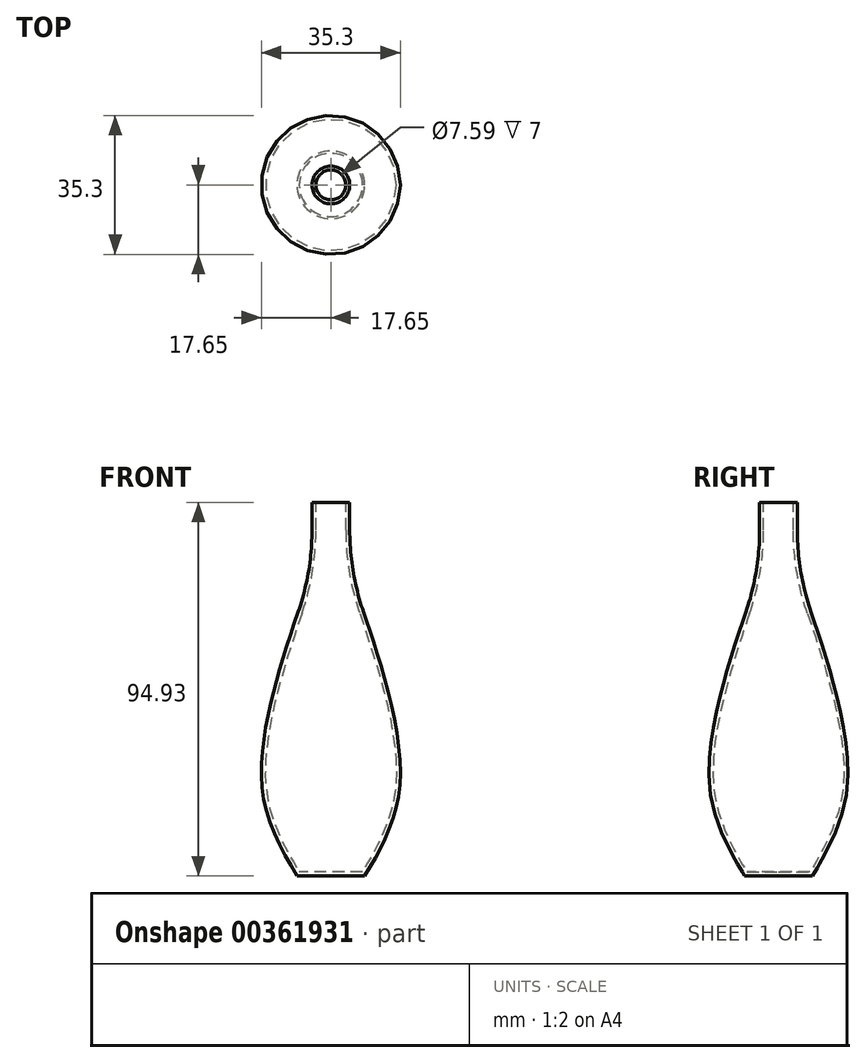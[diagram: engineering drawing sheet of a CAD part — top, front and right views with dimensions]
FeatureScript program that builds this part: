
annotation { "Feature Type Name" : "Feature", "Feature Type Description" : "" }
export const myFeature = defineFeature(function(context is Context, id is Id, definition is map)
    precondition{}
    {
        {
            var Q0;
            Q0=qCreatedBy(makeId("Front.planeOp"),FACE);
            var sketch = newSketch(context, id + "F0", { "sketchPlane" : qUnion([Q0])});
            skLineSegment(sketch, "E0", {"start": v(0, -43.14) * mm, "end": v(8.6, -43.14) * mm});
            skLineSegment(sketch, "E1", {"start": v(4.8, 43) * mm, "end": v(4.8, 51.79) * mm});
            skLineSegment(sketch, "E2", {"start": v(4.8, 51.79) * mm, "end": v(0, 51.79) * mm});
            skLineSegment(sketch, "E3", {"start": v(0, 55.64) * mm, "end": v(0, -43.14) * mm});
            skLineSegment(sketch, "E4", {"start": v(4.8, 33.68) * mm, "end": v(4.8, 43) * mm});
            skFitSpline(sketch, "E5", {"points": [v(4.8, 33.68) * mm, v(10.38, 17.7) * mm, v(17.57, -19.3) * mm, v(8.6, -43.14) * mm], "startDerivative": vector(18.72, -51.04) * mm, "endDerivative": vector(-38.07, -64.94) * mm});
            skSolve(sketch);
        }
        {
            var Q0;
            {var subQ1=sQuery(id+"F0.wireOp",EDGE,"E0");Q0=makeQuery(id+"F0.imprint","IMPRINT",FACE,{"disambiguationData":[TD([[makeQuery(id+"F0.imprint","IMPRINT",EDGE,{"derivedFrom":subQ1}),1.0]])]});}
            var Q1;
            Q1=sQuery(id+"F0.wireOp",EDGE,"E1");
            var Q2;
            Q2=sQuery(id+"F0.wireOp",EDGE,"E4");
            var Q3;
            Q3=sQuery(id+"F0.wireOp",EDGE,"E5");
            var Q4;
            Q4=sQuery(id+"F0.wireOp",EDGE,"E0");
            var Q5;
            Q5=sQuery(id+"F0.wireOp",EDGE,"E2");
            var Q6;
            Q6=sQuery(id+"F0.wireOp",EDGE,"E3");
            revolve(context, id + "F1", {"entities" : qUnion([Q0]), "surfaceEntities" : qUnion([Q1, Q2, Q3, Q4, Q5]), "axis" : qUnion([Q6]), "revolveType" : RevolveType.FULL});
        }
        {
            var Q0;
            Q0=makeQuery(id+"F1.opRevolve","SWEPT_EDGE",EDGE,{"disambiguationData":[OSD([sQuery(id+"F0.wireOp",VERTEX,"E5.start")])]});
            var Q1;
            Q1=makeQuery(id+"F1.opRevolve","SWEPT_EDGE",EDGE,{"disambiguationData":[OSD([sQuery(id+"F0.wireOp",EDGE,"E4"),sQuery(id+"F0.wireOp",EDGE,"E5")])]});
            fillet(context, id + "F2", {"entities" : qUnion([Q0, Q1]), "radius" : 63.93 * mm, "tangentPropagation" : true, "allowEdgeOverflow" : false});
        }
        {
            var Q0;
            Q0=makeQuery(id+"F1.opRevolve","SWEPT_FACE",FACE,{"disambiguationData":[OSD([sQuery(id+"F0.wireOp",EDGE,"E2")])]});
            shell(context, id + "F3", {"entities" : qUnion([Q0]), "thickness" : 1 * mm});
        }
    });
